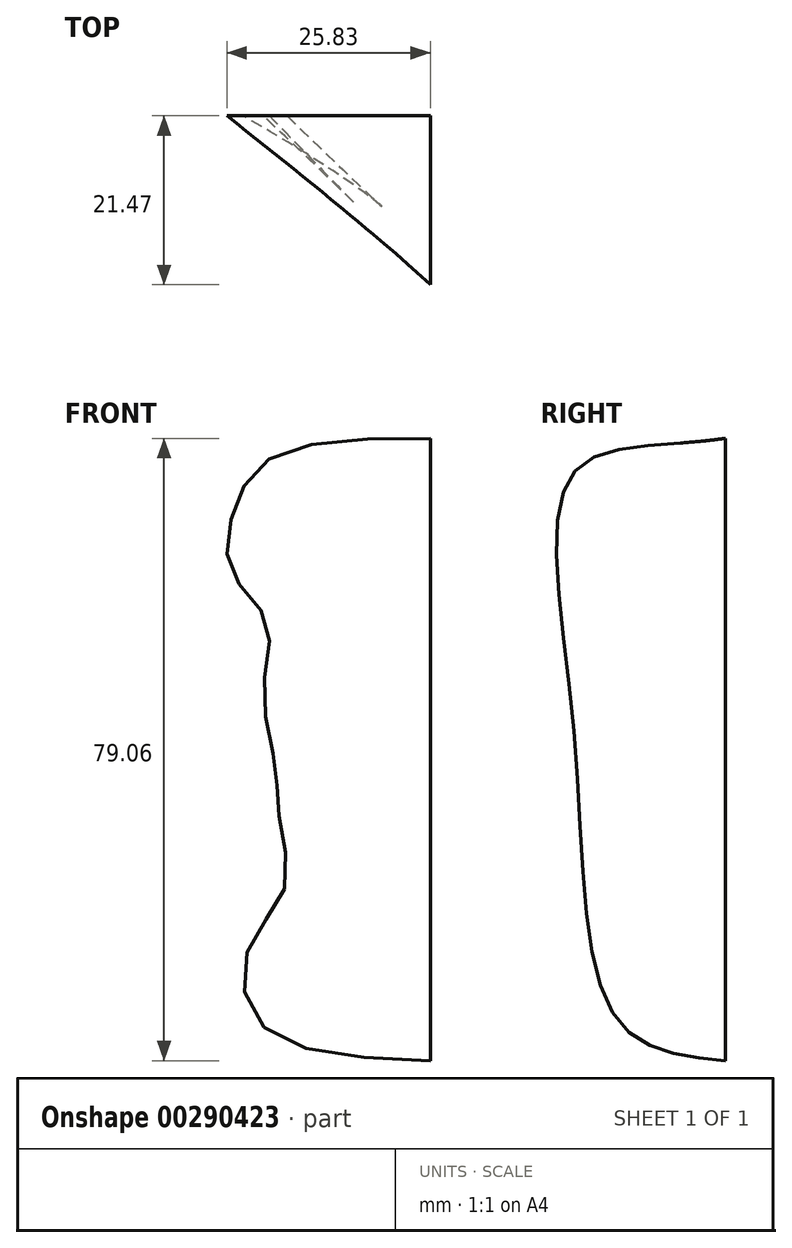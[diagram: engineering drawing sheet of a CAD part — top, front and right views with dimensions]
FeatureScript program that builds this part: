
annotation { "Feature Type Name" : "Feature", "Feature Type Description" : "" }
export const myFeature = defineFeature(function(context is Context, id is Id, definition is map)
    precondition{}
    {
        {
            var Q0;
            Q0=qCreatedBy(makeId("Front.planeOp"),FACE);
            var sketch = newSketch(context, id + "F0", { "sketchPlane" : qUnion([Q0])});
            skLineSegment(sketch, "E0", {"start": v(0, 0) * mm, "end": v(0, 79.05) * mm});
            skFitSpline(sketch, "E1", {"points": [v(0, 79.05) * mm, v(-20.2, 76.6) * mm, v(-25.12, 69.46) * mm, v(-25.12, 61.84) * mm, v(-20.7, 55.7) * mm, v(-21.19, 47.09) * mm, v(-19.71, 37.5) * mm, v(-19.22, 31.1) * mm, v(-18.48, 22) * mm, v(-23.16, 14.13) * mm, v(-21.19, 4.3) * mm, v(0, 0) * mm], "startDerivative": vector(-186.98, 0.35) * mm, "endDerivative": vector(197.15, -6.38) * mm});
            skSolve(sketch);
        }
        {
            var Q0;
            Q0=qCreatedBy(makeId("Right.planeOp"),FACE);
            var sketch = newSketch(context, id + "F1", { "sketchPlane" : qUnion([Q0])});
            skLineSegment(sketch, "E2.0", {"start": v(0, 0) * mm, "end": v(0, 79.05) * mm});
            skFitSpline(sketch, "E3", {"points": [v(0, 79.05) * mm, v(-19.13, 74.86) * mm, v(-19.24, 41.94) * mm, v(-13.58, 5.05) * mm, v(0, 0) * mm], "startDerivative": vector(-105.04, -16.16) * mm, "endDerivative": vector(80.25, -6.72) * mm});
            skSolve(sketch);
        }
        {
            var Q0;
            Q0=makeQuery(id+"F1.imprint","IMPRINT",FACE,{"disambiguationData":[TD([[makeQuery(id+"F1.imprint","IMPRINT",EDGE,{"derivedFrom":sQuery(id+"F1.wireOp",EDGE,"E2.0")}),1.0]])]});
            var Q1;
            Q1=makeQuery(id+"F0.imprint","IMPRINT",FACE,{"disambiguationData":[TD([[makeQuery(id+"F0.imprint","IMPRINT",EDGE,{"derivedFrom":sQuery(id+"F0.wireOp",EDGE,"E0")}),1.0]])]});
            var Q2;
            Q2=sQuery(id+"F0.wireOp",EDGE,"E1");
            var Q3;
            Q3=sQuery(id+"F1.wireOp",EDGE,"E3");
            loft(context, id + "F2", {"bodyType" : ToolBodyType.SURFACE, "sheetProfilesArray" : [{ "sheetProfileEntities" : qUnion([Q0]) }, { "sheetProfileEntities" : qUnion([Q1]) }], "wireProfilesArray" : [{ "wireProfileEntities" : qUnion([Q2]) }, { "wireProfileEntities" : qUnion([Q3]) }]});
        }
    });
